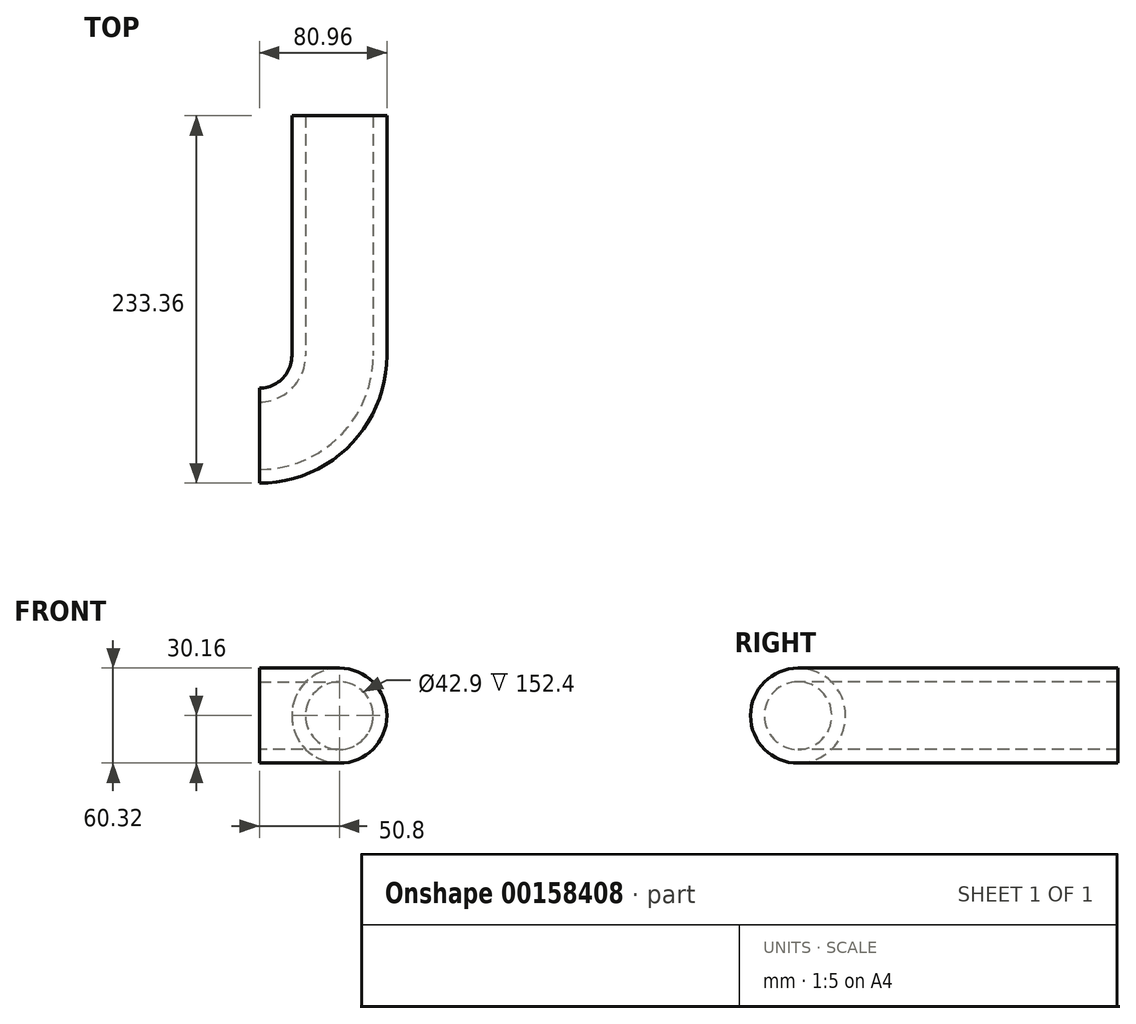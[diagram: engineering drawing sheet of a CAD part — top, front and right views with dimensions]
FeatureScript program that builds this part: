
annotation { "Feature Type Name" : "Feature", "Feature Type Description" : "" }
export const myFeature = defineFeature(function(context is Context, id is Id, definition is map)
    precondition{}
    {
        {
            var Q0;
            Q0=qCreatedBy(makeId("Front.planeOp"),FACE);
            var sketch = newSketch(context, id + "F0", { "sketchPlane" : qUnion([Q0])});
            skCircle(sketch, "E0", {"center": v(0, 0) * mm, "radius": 30.16 * mm});
            skCircle(sketch, "E1.0", {"center": v(0, 0) * mm, "radius": 21.45 * mm});
            skSolve(sketch);
        }
        {
            var Q0;
            Q0=qCreatedBy(makeId("Top.planeOp"),FACE);
            var sketch = newSketch(context, id + "F1", { "sketchPlane" : qUnion([Q0])});
            skLineSegment(sketch, "E2", {"start": v(0, 0) * mm, "end": v(0, -152.4) * mm});
            skLineSegment(sketch, "E3", {"start": v(0, -152.4) * mm, "end": v(-50.8, -152.4) * mm, "construction": true});
            skArc(sketch, "E4", {"start": v(0, -152.4) * mm, "mid": v(-14.88, -188.32) * mm, "end": v(-50.8, -203.2) * mm});
            skSolve(sketch);
        }
        {
            var Q0;
            Q0=makeQuery(id+"F0.imprint","IMPRINT",FACE,{"disambiguationData":[TD([[makeQuery(id+"F0.imprint","IMPRINT",EDGE,{"derivedFrom":sQuery(id+"F0.wireOp",EDGE,"E0")}),1.0]])]});
            var Q1;
            Q1=sQuery(id+"F1.wireOp",EDGE,"E2");
            var Q2;
            Q2=sQuery(id+"F1.wireOp",EDGE,"E4");
            sweep(context, id + "F2", {"profiles" : qUnion([Q0]), "path" : qUnion([Q1, Q2])});
        }
    });
